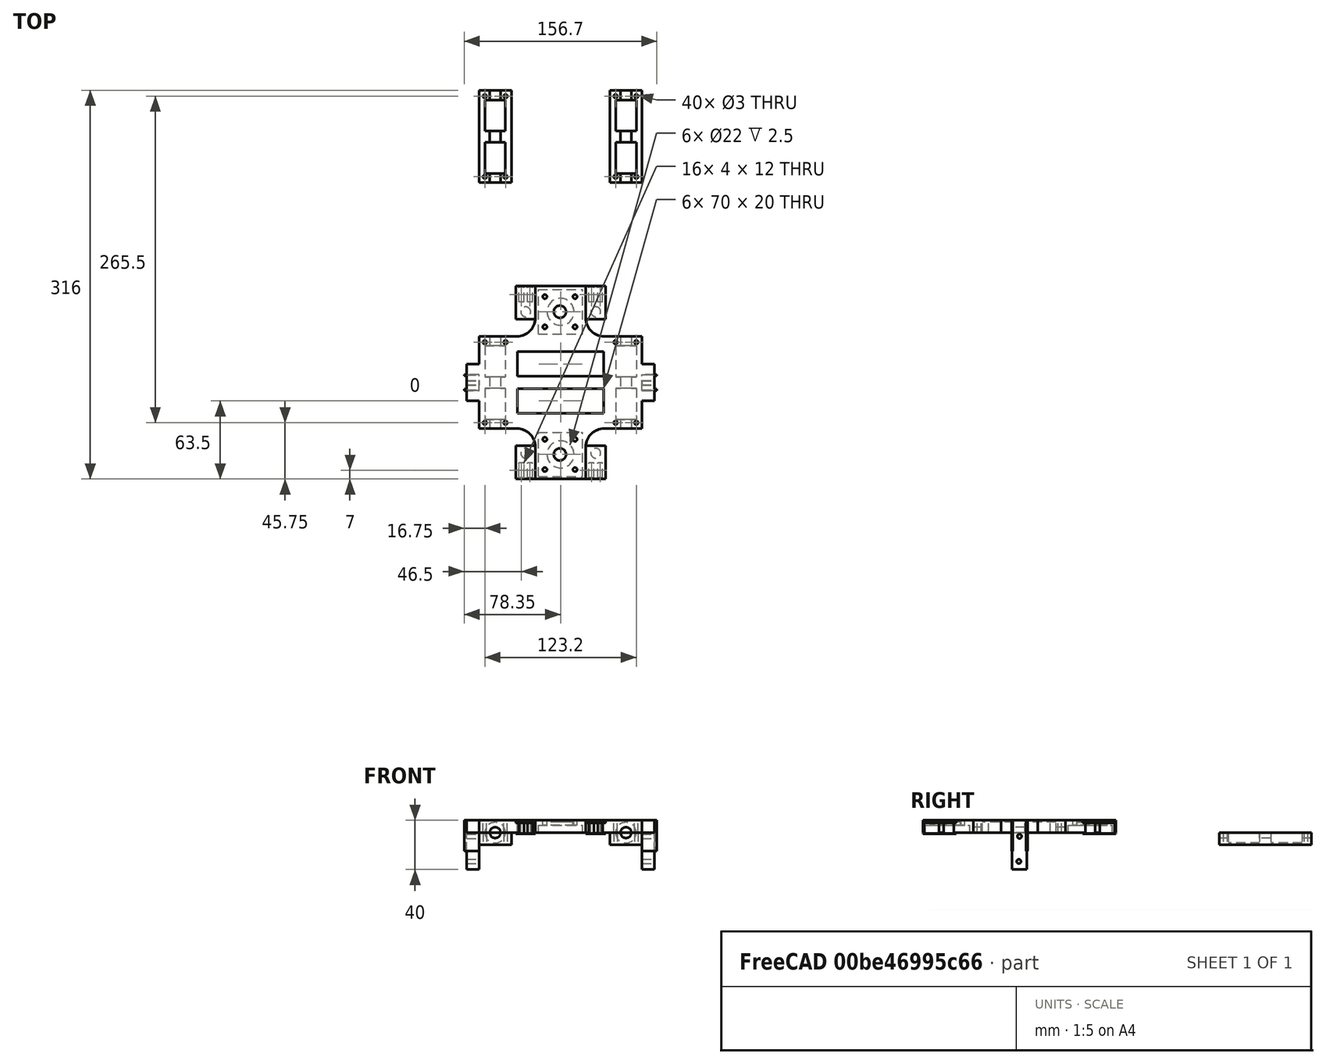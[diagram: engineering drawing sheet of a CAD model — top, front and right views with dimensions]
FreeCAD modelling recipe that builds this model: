
FCSTD DOCUMENT  (FreeCAD 0.16R6712 (Git))
Label: 1.4
License: All rights reserved
LicenseURL: http://en.wikipedia.org/wiki/All_rights_reserved
objects: Part::Cylinder×26, Part::Cut×26, Part::Box×21, Part::MultiFuse×13, Part::FeaturePython×9, Part::Fillet×4, Part::Feature×4, Part::Fuse×2
note: 105 computed .brp shape members not serialized (recipe doc carries the construction recipe); baked Part::Feature solids carry a one-line shape summary decoded from their .brp

FEATURE [Part::Box] Box  label="Cubo"
  Height = 10
  Length = 26.35
  Width = 75
FEATURE [Part::Cylinder] Cylinder  label="Cilindro"
  Angle = 360
  Height = 10
  Placement = pos=(4.75,4.75,0) rot=(0,0,1;0rad)
  Radius = 1.5
FEATURE [Part::Cylinder] Cylinder002  label="Cilindro002"
  Angle = 360
  Height = 10
  Placement = pos=(4.75,70.25,0) rot=(0,0,1;0rad)
  Radius = 1.5
FEATURE [Part::Cylinder] Cylinder003  label="Cilindro003"
  Angle = 360
  Height = 10
  Placement = pos=(21.6,4.75,0) rot=(0,0,1;0rad)
  Radius = 1.5
FEATURE [Part::Cut] Cut
  Base = -> Box
  Tool = -> Cylinder
FEATURE [Part::Cut] Cut001
  Base = -> Cut
  Tool = -> Cylinder002
FEATURE [Part::Cylinder] Cylinder004  label="Cilindro004"
  Angle = 360
  Height = 25.35
  Placement = pos=(13.175,30,0) rot=(1,0,0;1.5708rad)
  Radius = 8.4
FEATURE [Part::Cylinder] Cylinder005  label="Cilindro005"
  Angle = 360
  Height = 25.35
  Placement = pos=(13.175,64.5,0) rot=(1,0,0;1.5708rad)
  Radius = 8.4
FEATURE [Part::Cylinder] Cylinder006  label="Cilindro006"
  Angle = 360
  Height = 9.5
  Placement = pos=(13.175,39.5,0) rot=(1,0,0;1.5708rad)
  Radius = 4.4
FEATURE [Part::Fuse] Fusion
  Base = -> Cylinder004
  Tool = -> Cylinder005
FEATURE [Part::Fuse] Fusion001
  Base = -> Fusion
  Placement = pos=(0,2.75,0) rot=(0,0,1;0rad)
  Tool = -> Cylinder006
FEATURE [Part::Box] Box001  label="Centro"
  Height = 10
  Length = 80
  Placement = pos=(26.35,0,0) rot=(0,0,1;0rad)
  Width = 75
FEATURE [Part::Box] Box002  label="Lucernario"
  Height = 10
  Length = 70
  Placement = pos=(31.35,12.5,0) rot=(0,0,1;0rad)
  Width = 20
FEATURE [Part::Box] Box003  label="Lucernario2"
  Height = 10
  Length = 70
  Placement = pos=(31.35,42.5,0) rot=(0,0,1;0rad)
  Width = 20
FEATURE [Part::Cut] Cut007
  Base = -> Box001
  Tool = -> Box002
FEATURE [Part::Cut] Cut008  label="Centro1"
  Base = -> Cut007
  Tool = -> Box003
FEATURE [Part::Box] Box006  label="Guia1"
  Height = 10
  Length = 10
  Placement = pos=(-10,22.5,0) rot=(0,0,1;0rad)
  Width = 30
FEATURE [Part::Box] Box010  label="Cubo003"
  Height = 10
  Length = 26.35
  Width = 75
FEATURE [Part::Cylinder] Cylinder007  label="Cilindro007"
  Angle = 360
  Height = 25.35
  Placement = pos=(13.175,67.25,0) rot=(1,0,0;1.5708rad)
  Radius = 8.4
FEATURE [Part::Cut] Cut011
  Base = -> Box010
  Tool = -> Cylinder007
FEATURE [Part::Cylinder] Cylinder008  label="Cilindro008"
  Angle = 360
  Height = 9.5
  Placement = pos=(13.175,42.25,0) rot=(1,0,0;1.5708rad)
  Radius = 4.4
FEATURE [Part::Cut] Cut012
  Base = -> Cut011
  Tool = -> Cylinder008
FEATURE [Part::Cylinder] Cylinder009  label="Cilindro009"
  Angle = 360
  Height = 25.35
  Placement = pos=(13.175,32.75,0) rot=(1,0,0;1.5708rad)
  Radius = 8.4
FEATURE [Part::Cut] Cut013
  Base = -> Cut012
  Tool = -> Cylinder009
FEATURE [Part::Cylinder] Cylinder010  label="Cilindro010"
  Angle = 360
  Height = 10
  Placement = pos=(21.6,4.75,0) rot=(0,0,1;0rad)
  Radius = 1.5
FEATURE [Part::Cylinder] Cylinder011  label="Cilindro011"
  Angle = 360
  Height = 10
  Placement = pos=(4.75,4.75,0) rot=(0,0,1;0rad)
  Radius = 1.5
FEATURE [Part::Cut] Cut014
  Base = -> Cut013
  Tool = -> Cylinder010
FEATURE [Part::Cut] Cut015
  Base = -> Cut014
  Tool = -> Cylinder011
FEATURE [Part::Cylinder] Cylinder012  label="Cilindro012"
  Angle = 360
  Height = 10
  Placement = pos=(4.75,70.25,0) rot=(0,0,1;0rad)
  Radius = 1.5
FEATURE [Part::Cylinder] Cylinder013  label="Cilindro013"
  Angle = 360
  Height = 10
  Placement = pos=(21.6,70.25,0) rot=(0,0,1;0rad)
  Radius = 1.5
FEATURE [Part::Cut] Cut016
  Base = -> Cut015
  Tool = -> Cylinder012
FEATURE [Part::Cut] Cut017
  Base = -> Cut016
  Placement = pos=(0,0,0) rot=(0,1,0;3.14159rad)
  Tool = -> Cylinder013
FEATURE [Part::FeaturePython] Array001  label="Cierres"  # Draft array (typed FeaturePython)
  Angle = 360
  ArrayType = 0
  Axis = (0,0,1)
  Base = -> Cut017
  Center = (0,0,0)
  Fuse = false
  IntervalAxis = (0,0,0)
  IntervalX = (106.35,0,0)
  IntervalY = (0,1,0)
  IntervalZ = (0,0,0)
  NumberPolar = 1
  NumberX = 2
  NumberY = 1
  NumberZ = 1
  Placement = pos=(26.35,200,0) rot=(0,0,1;0rad)
FEATURE [Part::Box] Box011  label="Cubo004"
  Height = 10
  Length = 41
  Width = 41
FEATURE [Part::Cylinder] Cylinder014  label="Cilindro014"
  Angle = 360
  Height = 10
  Placement = pos=(7.7,7.7,0) rot=(0,0,1;0rad)
  Radius = 1.7
FEATURE [Part::Cylinder] Cylinder015  label="Cilindro015"
  Angle = 360
  Height = 10
  Placement = pos=(7.7,32.3,0) rot=(0,0,1;0rad)
  Radius = 1.7
FEATURE [Part::Cylinder] Cylinder016  label="Cilindro016"
  Angle = 360
  Height = 10
  Placement = pos=(32.3,7.7,0) rot=(0,0,1;0rad)
  Radius = 1.7
FEATURE [Part::Cylinder] Cylinder017  label="Cilindro017"
  Angle = 360
  Height = 10
  Placement = pos=(32.3,32.3,0) rot=(0,0,1;0rad)
  Radius = 1.7
FEATURE [Part::Cylinder] Cylinder018  label="Cilindro018"
  Angle = 360
  Height = 10
  Placement = pos=(20,20,0) rot=(0,0,1;0rad)
  Radius = 5
FEATURE [Part::Cut] Cut018
  Base = -> Box011
  Tool = -> Cylinder015
FEATURE [Part::Cut] Cut019
  Base = -> Cut018
  Tool = -> Cylinder014
FEATURE [Part::Cut] Cut020
  Base = -> Cut019
  Tool = -> Cylinder016
FEATURE [Part::Cut] Cut021
  Base = -> Cut020
  Tool = -> Cylinder017
FEATURE [Part::Cut] Cut022
  Base = -> Cut021
  Tool = -> Cylinder018
FEATURE [Part::Box] Box012  label="Cubo005"
  Height = 6
  Length = 36
  Placement = pos=(2.5,2,0) rot=(0,0,1;0rad)
  Width = 36
FEATURE [Part::Cut] Cut023
  Base = -> Cut022
  Placement = pos=(43.35,-46,0) rot=(0,0,1;0rad)
  Tool = -> Box012
FEATURE [Part::FeaturePython] Array002  # Draft array (typed FeaturePython)
  Angle = 360
  ArrayType = 0
  Axis = (0,0,1)
  Base = -> Cut023
  Center = (0,0,0)
  Fuse = false
  IntervalAxis = (0,0,0)
  IntervalX = (1,0,0)
  IntervalY = (0,116,0)
  IntervalZ = (0,0,0)
  NumberPolar = 1
  NumberX = 1
  NumberY = 2
  NumberZ = 1
  Placement = pos=(2.5,5,0) rot=(0,0,1;0rad)
FEATURE [Part::Box] Box014  label="Cubo007"
  Height = 25
  Length = 12
  Placement = pos=(132.7,31,-15) rot=(0,0,1;0rad)
  Width = 1
FEATURE [Part::Box] Box015  label="Cubo008"
  Height = 25
  Length = 12
  Placement = pos=(132.7,43,-15) rot=(0,0,1;0rad)
  Width = 1
FEATURE [Part::Box] Box016  label="Cubo009"
  Height = 30
  Length = 10
  Placement = pos=(-10,31.5,-30) rot=(0,0,1;0rad)
  Width = 12
FEATURE [Part::Box] Box017  label="Cubo010"
  Height = 25
  Length = 12
  Placement = pos=(-12,31,-15) rot=(0,0,1;0rad)
  Width = 1
FEATURE [Part::Box] Box018  label="Cubo011"
  Height = 25
  Length = 12
  Placement = pos=(-12,43,-15) rot=(0,0,1;0rad)
  Width = 1
FEATURE [Part::Cylinder] Cylinder019  label="Cilindro019"
  Angle = 360
  Height = 10
  Placement = pos=(-10,37.5,-3) rot=(0,1,0;1.5708rad)
  Radius = 1.75
FEATURE [Part::Cylinder] Cylinder020  label="Cilindro020"
  Angle = 360
  Height = 10
  Placement = pos=(-10,37,-23.5) rot=(0,1,0;1.5708rad)
  Radius = 1.75
FEATURE [Part::Cut] Cut024
  Base = -> Box016
  Tool = -> Cylinder020
FEATURE [Part::Cut] Cut025
  Base = -> Cut024
  Tool = -> Cylinder019
FEATURE [Part::FeaturePython] Array003  # Draft array (typed FeaturePython)
  Angle = 360
  ArrayType = 0
  Axis = (0,0,1)
  Base = -> Cut025
  Center = (0,0,0)
  Fuse = false
  IntervalAxis = (0,0,0)
  IntervalX = (142.7,0,0)
  IntervalY = (0,1,0)
  IntervalZ = (0,0,0)
  NumberPolar = 1
  NumberX = 2
  NumberY = 1
  NumberZ = 1
FEATURE [Part::MultiFuse] Fusion009
  Shapes = -> [Box015,Box014,Array003]
FEATURE [Part::MultiFuse] Fusion010
  Shapes = -> [Fusion009,Box018,Box017]
FEATURE [Part::Box] Box007  label="Guia2"
  Height = 10
  Length = 10
  Placement = pos=(132.7,22.5,0) rot=(0,0,1;0rad)
  Width = 30
FEATURE [Part::Cut] Cut026
  Base = -> Cut001
  Tool = -> Cylinder003
FEATURE [Part::Cylinder] Cylinder021  label="Cilindro021"
  Angle = 360
  Height = 10
  Placement = pos=(21.6,70.25,0) rot=(0,0,1;0rad)
  Radius = 1.5
FEATURE [Part::Cut] Cut027
  Base = -> Cut026
  Tool = -> Cylinder021
FEATURE [Part::Cut] Cut028
  Base = -> Cut027
  Tool = -> Fusion001
FEATURE [Part::FeaturePython] Array  # Draft array (typed FeaturePython)
  Angle = 360
  ArrayType = 0
  Axis = (0,0,1)
  Base = -> Cut028
  Center = (0,0,0)
  Fuse = false
  IntervalAxis = (0,0,0)
  IntervalX = (106.35,0,0)
  IntervalY = (0,1,0)
  IntervalZ = (0,0,0)
  NumberPolar = 1
  NumberX = 2
  NumberY = 1
  NumberZ = 1
FEATURE [Part::MultiFuse] Fusion011
  Shapes = -> [Array,Cut008]
FEATURE [Part::MultiFuse] Fusion012
  Shapes = -> [Array002,Fusion011]
FEATURE [Part::MultiFuse] Fusion013
  Shapes = -> [Fusion010,Fusion012]
FEATURE [Part::MultiFuse] Fusion014
  Shapes = -> [Box007,Fusion013]
FEATURE [Part::MultiFuse] Fusion015
  Shapes = -> [Box006,Fusion014]
FEATURE [Part::Fillet] Fillet
  Base = -> Fusion015
  Edges = 1 edges r=15: [Edge176]
FEATURE [Part::Fillet] Fillet001
  Base = -> Fillet
  Edges = 1 edges r=15: [Edge59]
FEATURE [Part::Fillet] Fillet002
  Base = -> Fillet001
  Edges = 1 edges r=15: [Edge73]
FEATURE [Part::Fillet] Fillet003
  Base = -> Fillet002
  Edges = 1 edges r=15: [Edge61]
FEATURE [Part::Cylinder] Cylinder022  label="Cilindro022"
  Angle = 360
  Height = 2.5
  Placement = pos=(66.35,-21,6) rot=(0,0,1;0rad)
  Radius = 11
FEATURE [Part::Cut] Cut029
  Base = -> Fillet003
  Tool = -> Cylinder022
FEATURE [Part::Cylinder] Cylinder023  label="Cilindro023"
  Angle = 360
  Height = 2.5
  Placement = pos=(66.35,95,6) rot=(0,0,1;0rad)
  Radius = 11
FEATURE [Part::Cut] Cut030
  Base = -> Cut029
  Tool = -> Cylinder023
FEATURE [Part::Feature] Cut030001  label="Cut031"
  shape: bbox 156.7 x 157 x 40 mm, 112 faces (baked)
FEATURE [Part::Feature] Array001001  label="Cierres001"
  shape: bbox 132.7 x 75 x 10 mm, 34 faces, 2 solids (baked)
FEATURE [Part::Cylinder] Cylinder024  label="Cilindro024"
  Angle = 360
  Height = 10
  Placement = pos=(38,-20,0) rot=(0,0,1;0rad)
  Radius = 4
FEATURE [Part::Box] Box019  label="Cubo012"
  Height = 0.2
  Length = 16
  Placement = pos=(29.85,-41,0) rot=(0,0,1;0rad)
  Width = 27
FEATURE [Part::MultiFuse] Fusion016
  Shapes = -> [Box019,Cylinder024]
FEATURE [Part::Box] Box020  label="Cubo013"
  Height = 10
  Length = 4
  Placement = pos=(32.5,-40,0) rot=(0,0,1;0rad)
  Width = 12
FEATURE [Part::Box] Box021  label="Cubo014"
  Height = 10
  Length = 4
  Placement = pos=(39.5,-40,0) rot=(0,0,1;0rad)
  Width = 12
FEATURE [Part::MultiFuse] Fusion017  label="Enganche"
  Shapes = -> [Box021,Box020,Fusion016]
FEATURE [Part::FeaturePython] Array001002  # Draft array (typed FeaturePython)
  Angle = 360
  ArrayType = 0
  Axis = (0,0,1)
  Base = -> Fusion017
  Center = (0,0,0)
  Fuse = false
  IntervalAxis = (0,0,0)
  IntervalX = (57,0,0)
  IntervalY = (0,1,0)
  IntervalZ = (0,0,0)
  NumberPolar = 1
  NumberX = 2
  NumberY = 1
  NumberZ = 1
  Placement = pos=(0,0,-1) rot=(0,0,1;0rad)
FEATURE [Part::Box] Box022  label="Cubo015"
  Height = 0.2
  Length = 16
  Placement = pos=(29.85,89,0) rot=(0,0,1;0rad)
  Width = 27
FEATURE [Part::Cylinder] Cylinder025  label="Cilindro025"
  Angle = 360
  Height = 10
  Placement = pos=(38,95,0) rot=(0,0,1;0rad)
  Radius = 4
FEATURE [Part::MultiFuse] Fusion018
  Shapes = -> [Cylinder025,Box022]
FEATURE [Part::Box] Box023  label="Cubo016"
  Height = 10
  Length = 4
  Placement = pos=(32.5,103,0) rot=(0,0,1;0rad)
  Width = 12
FEATURE [Part::Box] Box024  label="Cubo017"
  Height = 10
  Length = 4
  Placement = pos=(39.5,103,0) rot=(0,0,1;0rad)
  Width = 12
FEATURE [Part::MultiFuse] Fusion019
  Shapes = -> [Box023,Fusion018,Box024]
FEATURE [Part::FeaturePython] Array001003  # Draft array (typed FeaturePython)
  Angle = 360
  ArrayType = 0
  Axis = (0,0,1)
  Base = -> Fusion019
  Center = (0,0,0)
  Fuse = false
  IntervalAxis = (0,0,0)
  IntervalX = (57,0,0)
  IntervalY = (0,1,0)
  IntervalZ = (0,0,0)
  NumberPolar = 1
  NumberX = 2
  NumberY = 1
  NumberZ = 1
  Placement = pos=(0,0,-1) rot=(0,0,1;0rad)
FEATURE [Part::MultiFuse] Fusion020
  Shapes = -> [Cut030001,Array001003,Array001002]
FEATURE [Part::Box] Box025  label="Cubo018"
  Height = 2
  Length = 16
  Placement = pos=(29.85,89,9) rot=(0,0,1;0rad)
  Width = 27
FEATURE [Part::FeaturePython] Array001004  # Draft array (typed FeaturePython)
  Angle = 360
  ArrayType = 0
  Axis = (0,0,1)
  Base = -> Box025
  Center = (0,0,0)
  Fuse = false
  IntervalAxis = (0,0,0)
  IntervalX = (57,0,0)
  IntervalY = (0,1,0)
  IntervalZ = (0,0,0)
  NumberPolar = 1
  NumberX = 2
  NumberY = 1
  NumberZ = 1
FEATURE [Part::FeaturePython] Array001005  # Draft array (typed FeaturePython)
  Angle = 360
  ArrayType = 0
  Axis = (0,0,1)
  Base = -> Array001004
  Center = (0,0,0)
  Fuse = false
  IntervalAxis = (0,0,0)
  IntervalX = (1,0,0)
  IntervalY = (0,-130,0)
  IntervalZ = (0,0,0)
  NumberPolar = 1
  NumberX = 1
  NumberY = 2
  NumberZ = 1
  Placement = pos=(0,0,-1) rot=(0,0,1;0rad)
FEATURE [Part::Cylinder] Cylinder026  label="Cilindro026"
  Angle = 360
  Height = 300
  Placement = pos=(13.18,290,0) rot=(1,0,0;1.5708rad)
  Radius = 4.4
FEATURE [Part::FeaturePython] Array001006  # Draft array (typed FeaturePython)
  Angle = 360
  ArrayType = 0
  Axis = (0,0,1)
  Base = -> Cylinder026
  Center = (0,0,0)
  Fuse = false
  IntervalAxis = (0,0,0)
  IntervalX = (106.35,1,0)
  IntervalY = (0,1,0)
  IntervalZ = (0,0,0)
  NumberPolar = 1
  NumberX = 2
  NumberY = 1
  NumberZ = 1
FEATURE [Part::Cut] Cut030003
  Base = -> Array001001
  Tool = -> Array001006
FEATURE [Part::Feature] Cut030003001  label="Cut030004"
  shape: bbox 132.7 x 75 x 10 mm, 42 faces, 2 solids (baked)
FEATURE [Part::MultiFuse] Fusion021
  Shapes = -> [Array001005,Fusion020]
FEATURE [Part::Cut] Cut030003002
  Base = -> Fusion021
  Tool = -> Array001006
FEATURE [Part::Feature] Cut030003002001  label="Cut030003003"
  shape: bbox 156.7 x 157 x 40 mm, 192 faces (baked)
